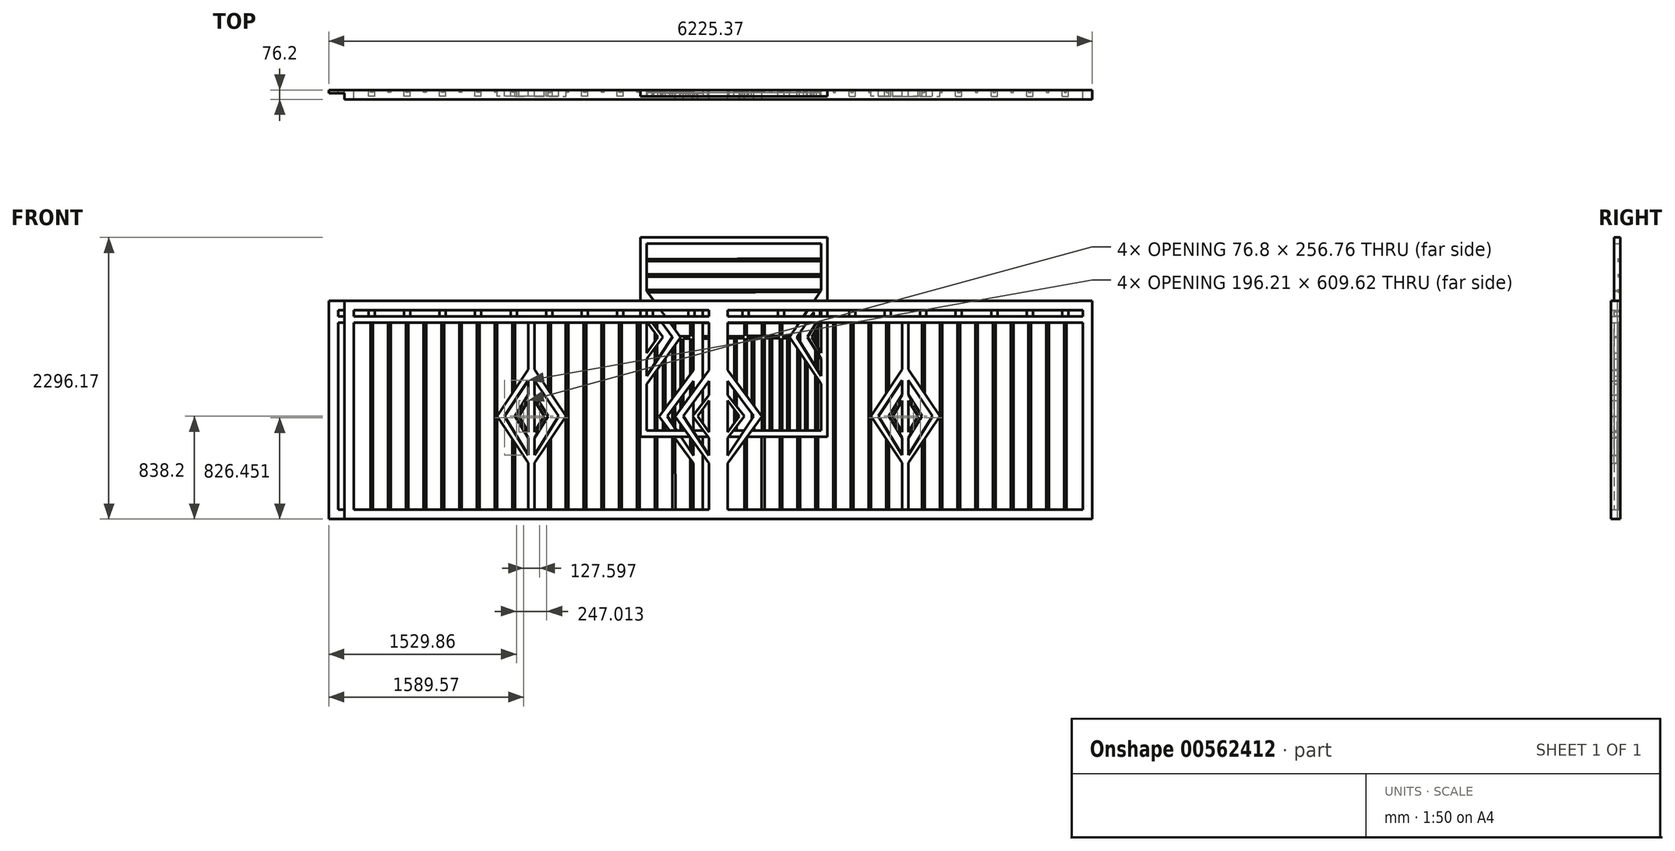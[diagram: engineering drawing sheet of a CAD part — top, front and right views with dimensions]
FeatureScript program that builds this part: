
annotation { "Feature Type Name" : "Feature", "Feature Type Description" : "" }
export const myFeature = defineFeature(function(context is Context, id is Id, definition is map)
    precondition{}
    {
        {
            var Q0;
            Q0=qCreatedBy(makeId("Front.planeOp"),FACE);
            var sketch = newSketch(context, id + "F0", { "sketchPlane" : qUnion([Q0])});
            skLineSegment(sketch, "E0.bottom", {"start": v(0, 0) * mm, "end": v(3048, 0) * mm});
            skLineSegment(sketch, "E0.top", {"start": v(0, -1778) * mm, "end": v(3048, -1778) * mm});
            skLineSegment(sketch, "E0.left", {"start": v(0, 0) * mm, "end": v(0, -1778) * mm});
            skLineSegment(sketch, "E0.right", {"start": v(3048, 0) * mm, "end": v(3048, -1778) * mm});
            skLineSegment(sketch, "E1.0", {"start": v(76.2, -76.2) * mm, "end": v(2971.8, -76.2) * mm});
            skLineSegment(sketch, "E1.1", {"start": v(76.2, -76.2) * mm, "end": v(76.2, -127) * mm});
            skLineSegment(sketch, "E1.2", {"start": v(76.2, -1701.8) * mm, "end": v(2971.8, -1701.8) * mm});
            skLineSegment(sketch, "E1.3", {"start": v(2971.8, -76.2) * mm, "end": v(2971.8, -127) * mm});
            skLineSegment(sketch, "E2.0", {"start": v(76.2, -127) * mm, "end": v(2971.8, -127) * mm});
            skLineSegment(sketch, "E3.0", {"start": v(76.2, -177.8) * mm, "end": v(2971.8, -177.8) * mm});
            skLineSegment(sketch, "E4.trimOffspring", {"start": v(76.2, -177.8) * mm, "end": v(76.2, -563.9) * mm});
            skLineSegment(sketch, "E5.trimOffspring", {"start": v(2971.8, -177.8) * mm, "end": v(2971.8, -1701.8) * mm});
            skLineSegment(sketch, "E6.0", {"start": v(1549.4, -177.8) * mm, "end": v(1549.4, -558.8) * mm});
            skLineSegment(sketch, "E7.0", {"start": v(2238.83, -177.8) * mm, "end": v(2238.83, -1701.8) * mm});
            skLineSegment(sketch, "E8.0", {"start": v(2257.88, -177.8) * mm, "end": v(2257.88, -1701.8) * mm});
            skLineSegment(sketch, "E9.1.0.0", {"start": v(2402.66, -177.8) * mm, "end": v(2402.66, -1701.8) * mm});
            skLineSegment(sketch, "E9.1.0.1", {"start": v(2383.61, -177.8) * mm, "end": v(2383.61, -1701.8) * mm});
            skLineSegment(sketch, "E9.2.0.0", {"start": v(2547.44, -177.8) * mm, "end": v(2547.44, -1701.8) * mm});
            skLineSegment(sketch, "E9.2.0.1", {"start": v(2528.4, -177.8) * mm, "end": v(2528.4, -1701.8) * mm});
            skLineSegment(sketch, "E9.3.0.0", {"start": v(2692.22, -177.8) * mm, "end": v(2692.22, -1701.8) * mm});
            skLineSegment(sketch, "E9.3.0.1", {"start": v(2673.17, -177.8) * mm, "end": v(2673.17, -1701.8) * mm});
            skLineSegment(sketch, "E9.4.0.0", {"start": v(2837, -177.8) * mm, "end": v(2837, -1701.8) * mm});
            skLineSegment(sketch, "E9.4.0.1", {"start": v(2817.95, -177.8) * mm, "end": v(2817.95, -1701.8) * mm});
            skLineSegment(sketch, "E9.direction1", {"start": v(2257.88, -1701.8) * mm, "end": v(2402.66, -1701.8) * mm, "construction": true});
            skLineSegment(sketch, "E10.MirrorCS", {"start": v(1949.27, -177.8) * mm, "end": v(1949.27, -1701.8) * mm});
            skLineSegment(sketch, "E11.MirrorCS", {"start": v(1659.71, -177.8) * mm, "end": v(1659.71, -723.56) * mm});
            skLineSegment(sketch, "E12.MirrorCS", {"start": v(2094.05, -177.8) * mm, "end": v(2094.05, -1701.8) * mm});
            skLineSegment(sketch, "E13.MirrorCS", {"start": v(2113.1, -177.8) * mm, "end": v(2113.1, -1701.8) * mm});
            skLineSegment(sketch, "E14.MirrorCS", {"start": v(1804.5, -177.8) * mm, "end": v(1804.5, -1701.8) * mm});
            skLineSegment(sketch, "E15.MirrorCS", {"start": v(1678.76, -177.8) * mm, "end": v(1678.76, -752.01) * mm});
            skLineSegment(sketch, "E16.MirrorCS", {"start": v(1968.32, -177.8) * mm, "end": v(1968.32, -1701.8) * mm});
            skLineSegment(sketch, "E17.MirrorCS", {"start": v(1823.54, -177.8) * mm, "end": v(1823.54, -1701.8) * mm});
            skLineSegment(sketch, "E18", {"start": v(1549.4, -558.8) * mm, "end": v(1804.5, -939.8) * mm});
            skLineSegment(sketch, "E19.MirrorCS", {"start": v(1549.4, -1320.8) * mm, "end": v(1804.5, -939.8) * mm});
            skLineSegment(sketch, "E20.MirrorCS", {"start": v(809.17, -177.8) * mm, "end": v(809.17, -1701.8) * mm});
            skLineSegment(sketch, "E21.MirrorCS", {"start": v(519.6, -177.8) * mm, "end": v(519.6, -1701.8) * mm});
            skLineSegment(sketch, "E22.MirrorCS", {"start": v(934.9, -177.8) * mm, "end": v(934.9, -1701.8) * mm});
            skLineSegment(sketch, "E23.MirrorCS", {"start": v(1243.5, -177.8) * mm, "end": v(1243.5, -1701.8) * mm});
            skLineSegment(sketch, "E24.MirrorCS", {"start": v(211, -177.8) * mm, "end": v(211, -746.81) * mm});
            skLineSegment(sketch, "E25.MirrorCS", {"start": v(953.95, -177.8) * mm, "end": v(953.95, -1701.8) * mm});
            skLineSegment(sketch, "E26.MirrorCS", {"start": v(374.83, -177.8) * mm, "end": v(374.83, -1701.8) * mm});
            skLineSegment(sketch, "E27.MirrorCS", {"start": v(1369.24, -177.8) * mm, "end": v(1369.24, -752.01) * mm});
            skLineSegment(sketch, "E28.MirrorCS", {"start": v(1498.6, -177.8) * mm, "end": v(1498.6, -558.8) * mm});
            skLineSegment(sketch, "E29.MirrorCS", {"start": v(645.34, -177.8) * mm, "end": v(645.34, -1701.8) * mm});
            skLineSegment(sketch, "E30.MirrorCS", {"start": v(500.56, -177.8) * mm, "end": v(500.56, -1701.8) * mm});
            skLineSegment(sketch, "E31.MirrorCS", {"start": v(1388.29, -177.8) * mm, "end": v(1388.29, -723.56) * mm});
            skLineSegment(sketch, "E32.MirrorCS", {"start": v(1079.68, -177.8) * mm, "end": v(1079.68, -1701.8) * mm});
            skLineSegment(sketch, "E33.MirrorCS", {"start": v(790.12, -177.8) * mm, "end": v(790.12, -1701.8) * mm});
            skLineSegment(sketch, "E34.MirrorCS", {"start": v(1224.46, -177.8) * mm, "end": v(1224.46, -1701.8) * mm});
            skLineSegment(sketch, "E35.MirrorCS", {"start": v(664.39, -177.8) * mm, "end": v(664.39, -1701.8) * mm});
            skLineSegment(sketch, "E36.MirrorCS", {"start": v(1098.73, -177.8) * mm, "end": v(1098.73, -1701.8) * mm});
            skLineSegment(sketch, "E37.MirrorCS", {"start": v(230.05, -177.8) * mm, "end": v(230.05, -772.66) * mm});
            skLineSegment(sketch, "E38.MirrorCS", {"start": v(355.78, -177.8) * mm, "end": v(352, -1703.62) * mm});
            skLineSegment(sketch, "E39", {"start": v(1549.4, -646.74) * mm, "end": v(1745.61, -939.8) * mm});
            skLineSegment(sketch, "E40", {"start": v(1745.61, -939.8) * mm, "end": v(1549.4, -1256.36) * mm});
            skLineSegment(sketch, "E41", {"start": v(1549.4, -811.42) * mm, "end": v(1626.2, -939.8) * mm});
            skLineSegment(sketch, "E42", {"start": v(1626.2, -939.8) * mm, "end": v(1549.4, -1068.18) * mm});
            skPoint(sketch, "E43.MirrorCS.end.orphan", {"position": v(1388.29, -939.8) * mm});
            skPoint(sketch, "E43.MirrorCS.start.orphan", {"position": v(1498.6, -1193.8) * mm});
            skPoint(sketch, "E44.MirrorCS.start.orphan", {"position": v(1498.6, -685.8) * mm});
            skPoint(sketch, "E45.orphan", {"position": v(1498.6, -558.8) * mm});
            skLineSegment(sketch, "E46", {"start": v(1549.4, -764.15) * mm, "end": v(1659.71, -939.8) * mm});
            skLineSegment(sketch, "E47", {"start": v(1659.71, -939.8) * mm, "end": v(1549.4, -1116.04) * mm});
            skLineSegment(sketch, "E48.MirrorCS", {"start": v(1421.8, -939.8) * mm, "end": v(1498.6, -1068.18) * mm});
            skLineSegment(sketch, "E49.MirrorCS", {"start": v(1388.29, -939.8) * mm, "end": v(1498.6, -1116.04) * mm});
            skLineSegment(sketch, "E50.MirrorCS", {"start": v(1498.6, -764.15) * mm, "end": v(1388.29, -939.8) * mm});
            skLineSegment(sketch, "E51.MirrorCS", {"start": v(1498.6, -811.42) * mm, "end": v(1421.8, -939.8) * mm});
            skLineSegment(sketch, "E52.MirrorCS", {"start": v(1498.6, -646.74) * mm, "end": v(1302.39, -939.8) * mm});
            skLineSegment(sketch, "E53.MirrorCS", {"start": v(1498.6, -558.8) * mm, "end": v(1243.5, -939.8) * mm});
            skLineSegment(sketch, "E54.MirrorCS", {"start": v(1498.6, -1320.8) * mm, "end": v(1243.5, -939.8) * mm});
            skLineSegment(sketch, "E55.MirrorCS", {"start": v(1302.39, -939.8) * mm, "end": v(1498.6, -1256.36) * mm});
            skLineSegment(sketch, "E56", {"start": v(76.2, -563.9) * mm, "end": v(353.89, -940.71) * mm});
            skLineSegment(sketch, "E57.MirrorCS", {"start": v(76.2, -1322.42) * mm, "end": v(353.89, -940.71) * mm});
            skLineSegment(sketch, "E58", {"start": v(74.38, -649.7) * mm, "end": v(288.17, -939.8) * mm});
            skLineSegment(sketch, "E59", {"start": v(288.17, -939.8) * mm, "end": v(76.2, -1257.98) * mm});
            skLineSegment(sketch, "E60", {"start": v(76.2, -813.05) * mm, "end": v(170.03, -939.8) * mm});
            skLineSegment(sketch, "E61", {"start": v(170.03, -939.8) * mm, "end": v(76.2, -1069.8) * mm});
            skLineSegment(sketch, "E62", {"start": v(76.2, -765.77) * mm, "end": v(211, -939.8) * mm});
            skLineSegment(sketch, "E63", {"start": v(211, -939.8) * mm, "end": v(76.2, -1117.66) * mm});
            skLineSegment(sketch, "E64.0", {"start": v(2852.88, -127) * mm, "end": v(2852.88, -76.2) * mm});
            skLineSegment(sketch, "E65.0", {"start": v(2802.08, -127) * mm, "end": v(2802.08, -76.2) * mm});
            skLineSegment(sketch, "E66.0", {"start": v(2563.32, -127) * mm, "end": v(2563.32, -76.2) * mm});
            skLineSegment(sketch, "E67.0", {"start": v(2512.52, -127) * mm, "end": v(2512.52, -76.2) * mm});
            skLineSegment(sketch, "E68.1.0.0", {"start": v(2222.96, -127) * mm, "end": v(2222.96, -76.2) * mm});
            skLineSegment(sketch, "E68.1.0.1", {"start": v(2273.76, -127) * mm, "end": v(2273.76, -76.2) * mm});
            skLineSegment(sketch, "E68.2.0.0", {"start": v(1933.4, -127) * mm, "end": v(1933.4, -76.2) * mm});
            skLineSegment(sketch, "E68.2.0.1", {"start": v(1984.2, -127) * mm, "end": v(1984.2, -76.2) * mm});
            skLineSegment(sketch, "E68.3.0.0", {"start": v(1643.84, -127) * mm, "end": v(1643.84, -76.2) * mm});
            skLineSegment(sketch, "E68.3.0.1", {"start": v(1694.64, -127) * mm, "end": v(1694.64, -76.2) * mm});
            skLineSegment(sketch, "E68.4.0.0", {"start": v(1354.28, -127) * mm, "end": v(1354.28, -76.2) * mm});
            skLineSegment(sketch, "E68.4.0.1", {"start": v(1405.08, -127) * mm, "end": v(1405.08, -76.2) * mm});
            skLineSegment(sketch, "E68.5.0.0", {"start": v(1064.72, -127) * mm, "end": v(1064.72, -76.2) * mm});
            skLineSegment(sketch, "E68.5.0.1", {"start": v(1115.52, -127) * mm, "end": v(1115.52, -76.2) * mm});
            skLineSegment(sketch, "E68.6.0.0", {"start": v(775.16, -127) * mm, "end": v(775.16, -76.2) * mm});
            skLineSegment(sketch, "E68.6.0.1", {"start": v(825.96, -127) * mm, "end": v(825.96, -76.2) * mm});
            skLineSegment(sketch, "E68.7.0.0", {"start": v(485.6, -127) * mm, "end": v(485.6, -76.2) * mm});
            skLineSegment(sketch, "E68.7.0.1", {"start": v(536.4, -127) * mm, "end": v(536.4, -76.2) * mm});
            skLineSegment(sketch, "E68.8.0.0", {"start": v(196.04, -127) * mm, "end": v(196.04, -76.2) * mm});
            skLineSegment(sketch, "E68.8.0.1", {"start": v(246.84, -127) * mm, "end": v(246.84, -76.2) * mm});
            skLineSegment(sketch, "E68.direction1", {"start": v(2512.52, -127) * mm, "end": v(2222.96, -127) * mm, "construction": true});
            skLineSegment(sketch, "E69", {"start": v(-64.68, 459.45) * mm, "end": v(-64.68, -2374.18) * mm});
            skLineSegment(sketch, "E70.trimOffspring", {"start": v(1388.29, -1156.04) * mm, "end": v(1388.29, -1701.8) * mm});
            skLineSegment(sketch, "E71.trimOffspring", {"start": v(1369.24, -1127.59) * mm, "end": v(1369.24, -1701.8) * mm});
            skLineSegment(sketch, "E72.trimOffspring", {"start": v(1659.71, -1156.04) * mm, "end": v(1659.71, -1701.8) * mm});
            skLineSegment(sketch, "E73.trimOffspring", {"start": v(1678.76, -1127.59) * mm, "end": v(1678.76, -1701.8) * mm});
            skLineSegment(sketch, "E74.trimOffspring", {"start": v(1498.6, -646.74) * mm, "end": v(1498.6, -764.15) * mm});
            skLineSegment(sketch, "E75.trimOffspring", {"start": v(1549.4, -646.74) * mm, "end": v(1549.4, -764.15) * mm});
            skLineSegment(sketch, "E76.trimOffspring", {"start": v(1498.6, -811.42) * mm, "end": v(1498.6, -1068.18) * mm});
            skLineSegment(sketch, "E77.trimOffspring", {"start": v(1549.4, -811.42) * mm, "end": v(1549.4, -1068.18) * mm});
            skLineSegment(sketch, "E78.trimOffspring", {"start": v(1498.6, -1116.04) * mm, "end": v(1498.6, -1256.36) * mm});
            skLineSegment(sketch, "E79.trimOffspring", {"start": v(1549.4, -1116.04) * mm, "end": v(1549.4, -1256.36) * mm});
            skLineSegment(sketch, "E80.trimOffspring", {"start": v(1498.6, -1320.8) * mm, "end": v(1498.6, -1701.8) * mm});
            skLineSegment(sketch, "E81.trimOffspring", {"start": v(1549.4, -1320.8) * mm, "end": v(1549.4, -1701.8) * mm});
            skLineSegment(sketch, "E82.trimOffspring", {"start": v(230.05, -1110.94) * mm, "end": v(230.05, -1701.8) * mm});
            skLineSegment(sketch, "E83.trimOffspring", {"start": v(211, -1137.13) * mm, "end": v(211, -1701.8) * mm});
            skLineSegment(sketch, "E84.trimOffspring", {"start": v(76.2, -652.17) * mm, "end": v(76.2, -765.77) * mm});
            skLineSegment(sketch, "E85.trimOffspring", {"start": v(76.2, -813.05) * mm, "end": v(76.2, -1069.8) * mm});
            skLineSegment(sketch, "E86.trimOffspring", {"start": v(76.2, -1117.66) * mm, "end": v(76.2, -1701.8) * mm});
            skLineSegment(sketch, "E87.MirrorCS", {"start": v(-3101.17, -76.2) * mm, "end": v(-3101.17, -127) * mm});
            skLineSegment(sketch, "E88.MirrorCS", {"start": v(-1627.97, -646.74) * mm, "end": v(-1627.97, -764.15) * mm});
            skLineSegment(sketch, "E89.MirrorCS", {"start": v(-1678.77, -646.74) * mm, "end": v(-1678.77, -764.15) * mm});
            skLineSegment(sketch, "E90.MirrorCS", {"start": v(-1627.97, -1116.04) * mm, "end": v(-1627.97, -1256.36) * mm});
            skLineSegment(sketch, "E91.MirrorCS", {"start": v(-1678.77, -1116.04) * mm, "end": v(-1678.77, -1256.36) * mm});
            skLineSegment(sketch, "E92.MirrorCS", {"start": v(-2692.69, -127) * mm, "end": v(-2692.69, -76.2) * mm});
            skLineSegment(sketch, "E93.MirrorCS", {"start": v(-1627.97, -764.15) * mm, "end": v(-1517.66, -939.8) * mm});
            skLineSegment(sketch, "E94.MirrorCS", {"start": v(-2641.89, -127) * mm, "end": v(-2641.89, -76.2) * mm});
            skLineSegment(sketch, "E95.MirrorCS", {"start": v(-1627.97, -811.42) * mm, "end": v(-1551.17, -939.8) * mm});
            skLineSegment(sketch, "E96.MirrorCS", {"start": v(-2062.77, -127) * mm, "end": v(-2062.77, -76.2) * mm});
            skLineSegment(sketch, "E97.MirrorCS", {"start": v(-205.57, -76.2) * mm, "end": v(-205.57, -127) * mm});
            skLineSegment(sketch, "E98.MirrorCS", {"start": v(-205.57, -652.17) * mm, "end": v(-205.57, -765.77) * mm});
            skLineSegment(sketch, "E99.MirrorCS", {"start": v(-2352.33, -127) * mm, "end": v(-2352.33, -76.2) * mm});
            skLineSegment(sketch, "E100.MirrorCS", {"start": v(-1773.2, -127) * mm, "end": v(-1773.2, -76.2) * mm});
            skLineSegment(sketch, "E101.MirrorCS", {"start": v(-2403.13, -127) * mm, "end": v(-2403.13, -76.2) * mm});
            skLineSegment(sketch, "E102.MirrorCS", {"start": v(-2113.57, -127) * mm, "end": v(-2113.57, -76.2) * mm});
            skLineSegment(sketch, "E103.MirrorCS", {"start": v(-205.57, -813.05) * mm, "end": v(-299.4, -939.8) * mm});
            skLineSegment(sketch, "E104.MirrorCS", {"start": v(-1678.77, -811.42) * mm, "end": v(-1755.57, -939.8) * mm});
            skLineSegment(sketch, "E105.MirrorCS", {"start": v(-2368.2, -177.8) * mm, "end": v(-2368.2, -1701.8) * mm});
            skLineSegment(sketch, "E106.MirrorCS", {"start": v(-299.4, -939.8) * mm, "end": v(-205.57, -1069.8) * mm});
            skLineSegment(sketch, "E107.MirrorCS", {"start": v(-1755.57, -939.8) * mm, "end": v(-1678.77, -1068.18) * mm});
            skLineSegment(sketch, "E108.MirrorCS", {"start": v(-904.53, -127) * mm, "end": v(-904.53, -76.2) * mm});
            skLineSegment(sketch, "E109.MirrorCS", {"start": v(-955.33, -127) * mm, "end": v(-955.33, -76.2) * mm});
            skLineSegment(sketch, "E110.MirrorCS", {"start": v(-614.97, -127) * mm, "end": v(-614.97, -76.2) * mm});
            skLineSegment(sketch, "E111.MirrorCS", {"start": v(-1551.17, -939.8) * mm, "end": v(-1627.97, -1068.18) * mm});
            skLineSegment(sketch, "E112.MirrorCS", {"start": v(-665.77, -127) * mm, "end": v(-665.77, -76.2) * mm});
            skLineSegment(sketch, "E113.MirrorCS", {"start": v(-1517.66, -939.8) * mm, "end": v(-1627.97, -1116.04) * mm});
            skLineSegment(sketch, "E114.MirrorCS", {"start": v(-359.42, -1110.94) * mm, "end": v(-359.42, -1701.8) * mm});
            skLineSegment(sketch, "E115.MirrorCS", {"start": v(-325.4, -127) * mm, "end": v(-325.4, -76.2) * mm});
            skLineSegment(sketch, "E116.MirrorCS", {"start": v(-376.2, -127) * mm, "end": v(-376.2, -76.2) * mm});
            skLineSegment(sketch, "E117.MirrorCS", {"start": v(-205.57, -1701.8) * mm, "end": v(-3101.17, -1701.8) * mm});
            skLineSegment(sketch, "E118.MirrorCS", {"start": v(-205.57, -127) * mm, "end": v(-3101.17, -127) * mm});
            skLineSegment(sketch, "E119.MirrorCS", {"start": v(-205.57, -177.8) * mm, "end": v(-3101.17, -177.8) * mm});
            skLineSegment(sketch, "E120.MirrorCS", {"start": v(-2641.89, -127) * mm, "end": v(-2352.33, -127) * mm, "construction": true});
            skLineSegment(sketch, "E121.MirrorCS", {"start": v(-359.42, -177.8) * mm, "end": v(-359.42, -772.66) * mm});
            skLineSegment(sketch, "E122.MirrorCS", {"start": v(-1824, -127) * mm, "end": v(-1824, -76.2) * mm});
            skLineSegment(sketch, "E123.MirrorCS", {"start": v(-2387.25, -1701.8) * mm, "end": v(-2532.03, -1701.8) * mm, "construction": true});
            skLineSegment(sketch, "E124.MirrorCS", {"start": v(-1483.65, -127) * mm, "end": v(-1483.65, -76.2) * mm});
            skPoint(sketch, "E125.MirrorP", {"position": v(-1517.66, -939.8) * mm});
            skLineSegment(sketch, "E126.MirrorCS", {"start": v(-1534.45, -127) * mm, "end": v(-1534.45, -76.2) * mm});
            skLineSegment(sketch, "E127.MirrorCS", {"start": v(-1194.09, -127) * mm, "end": v(-1194.09, -76.2) * mm});
            skLineSegment(sketch, "E128.MirrorCS", {"start": v(-1228.1, -177.8) * mm, "end": v(-1228.1, -1701.8) * mm});
            skLineSegment(sketch, "E129.MirrorCS", {"start": v(-1244.89, -127) * mm, "end": v(-1244.89, -76.2) * mm});
            skLineSegment(sketch, "E130.MirrorCS", {"start": v(-2802.54, -177.8) * mm, "end": v(-2802.54, -1701.8) * mm});
            skLineSegment(sketch, "E131.MirrorCS", {"start": v(-938.54, -177.8) * mm, "end": v(-938.54, -1701.8) * mm});
            skLineSegment(sketch, "E132.MirrorCS", {"start": v(-774.7, -177.8) * mm, "end": v(-774.7, -1701.8) * mm});
            skLineSegment(sketch, "E133.MirrorCS", {"start": v(-2982.25, -127) * mm, "end": v(-2982.25, -76.2) * mm});
            skLineSegment(sketch, "E134.MirrorCS", {"start": v(-2931.45, -127) * mm, "end": v(-2931.45, -76.2) * mm});
            skLineSegment(sketch, "E135.MirrorCS", {"start": v(-1517.66, -177.8) * mm, "end": v(-1517.66, -723.56) * mm});
            skLineSegment(sketch, "E136.MirrorCS", {"start": v(-2097.7, -177.8) * mm, "end": v(-2097.7, -1701.8) * mm});
            skLineSegment(sketch, "E137.MirrorCS", {"start": v(-340.37, -1137.13) * mm, "end": v(-340.37, -1701.8) * mm});
            skLineSegment(sketch, "E138.MirrorCS", {"start": v(-1209.05, -177.8) * mm, "end": v(-1209.05, -1701.8) * mm});
            skLineSegment(sketch, "E139.MirrorCS", {"start": v(-1952.91, -177.8) * mm, "end": v(-1952.91, -1701.8) * mm});
            skLineSegment(sketch, "E140.MirrorCS", {"start": v(-2512.98, -177.8) * mm, "end": v(-2512.98, -1701.8) * mm});
            skLineSegment(sketch, "E141.MirrorCS", {"start": v(-1498.6, -1127.59) * mm, "end": v(-1498.6, -1701.8) * mm});
            skLineSegment(sketch, "E142.MirrorCS", {"start": v(-2387.25, -177.8) * mm, "end": v(-2387.25, -1701.8) * mm});
            skLineSegment(sketch, "E143.MirrorCS", {"start": v(-2532.03, -177.8) * mm, "end": v(-2532.03, -1701.8) * mm});
            skLineSegment(sketch, "E144.MirrorCS", {"start": v(-793.76, -177.8) * mm, "end": v(-793.76, -1701.8) * mm});
            skLineSegment(sketch, "E145.MirrorCS", {"start": v(-129.37, 0) * mm, "end": v(-3177.37, 0) * mm});
            skLineSegment(sketch, "E146.MirrorCS", {"start": v(-129.37, -1778) * mm, "end": v(-3177.37, -1778) * mm});
            skLineSegment(sketch, "E147.MirrorCS", {"start": v(-2821.6, -177.8) * mm, "end": v(-2821.6, -1701.8) * mm});
            skLineSegment(sketch, "E148.MirrorCS", {"start": v(-205.57, -1117.66) * mm, "end": v(-205.57, -1701.8) * mm});
            skLineSegment(sketch, "E149.MirrorCS", {"start": v(-1517.66, -1156.04) * mm, "end": v(-1517.66, -1701.8) * mm});
            skLineSegment(sketch, "E150.MirrorCS", {"start": v(-1627.97, -1320.8) * mm, "end": v(-1372.88, -939.8) * mm});
            skLineSegment(sketch, "E151.MirrorCS", {"start": v(-129.37, 0) * mm, "end": v(-129.37, -1778) * mm});
            skLineSegment(sketch, "E152.MirrorCS", {"start": v(-3177.37, 0) * mm, "end": v(-3177.37, -1778) * mm});
            skLineSegment(sketch, "E153.MirrorCS", {"start": v(-205.57, -76.2) * mm, "end": v(-3101.17, -76.2) * mm});
            skLineSegment(sketch, "E154.MirrorCS", {"start": v(-205.57, -177.8) * mm, "end": v(-205.57, -563.9) * mm});
            skLineSegment(sketch, "E155.MirrorCS", {"start": v(-3101.17, -177.8) * mm, "end": v(-3101.17, -1701.8) * mm});
            skLineSegment(sketch, "E156.MirrorCS", {"start": v(-919.49, -177.8) * mm, "end": v(-919.49, -1701.8) * mm});
            skLineSegment(sketch, "E157.MirrorCS", {"start": v(-1678.77, -558.8) * mm, "end": v(-1933.86, -939.8) * mm});
            skLineSegment(sketch, "E158.MirrorCS", {"start": v(-2676.81, -177.8) * mm, "end": v(-2676.81, -1701.8) * mm});
            skLineSegment(sketch, "E159.MirrorCS", {"start": v(-1678.77, -177.8) * mm, "end": v(-1678.77, -558.8) * mm});
            skLineSegment(sketch, "E160.MirrorCS", {"start": v(-1431.76, -939.8) * mm, "end": v(-1627.97, -1256.36) * mm});
            skLineSegment(sketch, "E161.MirrorCS", {"start": v(-1627.97, -646.74) * mm, "end": v(-1431.76, -939.8) * mm});
            skLineSegment(sketch, "E162.MirrorCS", {"start": v(-1064.27, -177.8) * mm, "end": v(-1064.27, -1701.8) * mm});
            skLineSegment(sketch, "E163.MirrorCS", {"start": v(-2966.37, -177.8) * mm, "end": v(-2966.37, -1701.8) * mm});
            skLineSegment(sketch, "E164.MirrorCS", {"start": v(-1789.08, -1156.04) * mm, "end": v(-1789.08, -1701.8) * mm});
            skLineSegment(sketch, "E165.MirrorCS", {"start": v(-205.57, -563.9) * mm, "end": v(-483.26, -940.71) * mm});
            skLineSegment(sketch, "E166.MirrorCS", {"start": v(-485.15, -177.8) * mm, "end": v(-481.37, -1703.62) * mm});
            skLineSegment(sketch, "E167.MirrorCS", {"start": v(-1372.88, -177.8) * mm, "end": v(-1372.88, -1701.8) * mm});
            skLineSegment(sketch, "E168.MirrorCS", {"start": v(-2947.32, -177.8) * mm, "end": v(-2947.32, -1701.8) * mm});
            skLineSegment(sketch, "E169.MirrorCS", {"start": v(-1808.13, -1127.59) * mm, "end": v(-1808.13, -1701.8) * mm});
            skLineSegment(sketch, "E170.MirrorCS", {"start": v(-205.57, -1322.42) * mm, "end": v(-483.26, -940.71) * mm});
            skLineSegment(sketch, "E171.MirrorCS", {"start": v(-205.57, -813.05) * mm, "end": v(-205.57, -1069.8) * mm});
            skLineSegment(sketch, "E172.MirrorCS", {"start": v(-203.75, -649.7) * mm, "end": v(-417.54, -939.8) * mm});
            skLineSegment(sketch, "E173.MirrorCS", {"start": v(-1678.77, -646.74) * mm, "end": v(-1874.98, -939.8) * mm});
            skLineSegment(sketch, "E174.MirrorCS", {"start": v(-1627.97, -558.8) * mm, "end": v(-1372.88, -939.8) * mm});
            skLineSegment(sketch, "E175.MirrorCS", {"start": v(-340.37, -177.8) * mm, "end": v(-340.37, -746.81) * mm});
            skLineSegment(sketch, "E176.MirrorCS", {"start": v(-2078.64, -177.8) * mm, "end": v(-2078.64, -1701.8) * mm});
            skLineSegment(sketch, "E177.MirrorCS", {"start": v(-417.54, -939.8) * mm, "end": v(-205.57, -1257.98) * mm});
            skLineSegment(sketch, "E178.MirrorCS", {"start": v(-1874.98, -939.8) * mm, "end": v(-1678.77, -1256.36) * mm});
            skLineSegment(sketch, "E179.MirrorCS", {"start": v(-1083.32, -177.8) * mm, "end": v(-1083.32, -1701.8) * mm});
            skPoint(sketch, "E180.MirrorP", {"position": v(-1627.97, -1193.8) * mm});
            skLineSegment(sketch, "E181.MirrorCS", {"start": v(-1789.08, -177.8) * mm, "end": v(-1789.08, -723.56) * mm});
            skLineSegment(sketch, "E182.MirrorCS", {"start": v(-504.2, -177.8) * mm, "end": v(-504.2, -1701.8) * mm});
            skLineSegment(sketch, "E183.MirrorCS", {"start": v(-1627.97, -811.42) * mm, "end": v(-1627.97, -1068.18) * mm});
            skLineSegment(sketch, "E184.MirrorCS", {"start": v(-648.98, -177.8) * mm, "end": v(-648.98, -1701.8) * mm});
            skLineSegment(sketch, "E185.MirrorCS", {"start": v(-1498.6, -177.8) * mm, "end": v(-1498.6, -752.01) * mm});
            skLineSegment(sketch, "E186.MirrorCS", {"start": v(-1678.77, -811.42) * mm, "end": v(-1678.77, -1068.18) * mm});
            skLineSegment(sketch, "E187.MirrorCS", {"start": v(-2223.42, -177.8) * mm, "end": v(-2223.42, -1701.8) * mm});
            skLineSegment(sketch, "E188.MirrorCS", {"start": v(-1353.83, -177.8) * mm, "end": v(-1353.83, -1701.8) * mm});
            skLineSegment(sketch, "E189.MirrorCS", {"start": v(-205.57, -765.77) * mm, "end": v(-340.37, -939.8) * mm});
            skLineSegment(sketch, "E190.MirrorCS", {"start": v(-1678.77, -764.15) * mm, "end": v(-1789.08, -939.8) * mm});
            skLineSegment(sketch, "E191.MirrorCS", {"start": v(-1627.97, -177.8) * mm, "end": v(-1627.97, -558.8) * mm});
            skPoint(sketch, "E192.MirrorP", {"position": v(-1627.97, -685.8) * mm});
            skLineSegment(sketch, "E193.MirrorCS", {"start": v(-2242.47, -177.8) * mm, "end": v(-2242.47, -1701.8) * mm});
            skLineSegment(sketch, "E194.MirrorCS", {"start": v(-340.37, -939.8) * mm, "end": v(-205.57, -1117.66) * mm});
            skLineSegment(sketch, "E195.MirrorCS", {"start": v(-1789.08, -939.8) * mm, "end": v(-1678.77, -1116.04) * mm});
            skLineSegment(sketch, "E196.MirrorCS", {"start": v(-1678.77, -1320.8) * mm, "end": v(-1933.86, -939.8) * mm});
            skPoint(sketch, "E197.MirrorP", {"position": v(-1627.97, -558.8) * mm});
            skLineSegment(sketch, "E198.MirrorCS", {"start": v(-2657.76, -177.8) * mm, "end": v(-2657.76, -1701.8) * mm});
            skLineSegment(sketch, "E199.MirrorCS", {"start": v(-1933.86, -177.8) * mm, "end": v(-1933.86, -1701.8) * mm});
            skLineSegment(sketch, "E200.MirrorCS", {"start": v(-1627.97, -1320.8) * mm, "end": v(-1627.97, -1701.8) * mm});
            skLineSegment(sketch, "E201.MirrorCS", {"start": v(-629.93, -177.8) * mm, "end": v(-629.93, -1701.8) * mm});
            skLineSegment(sketch, "E202.MirrorCS", {"start": v(-1808.13, -177.8) * mm, "end": v(-1808.13, -752.01) * mm});
            skLineSegment(sketch, "E203.MirrorCS", {"start": v(-1678.77, -1320.8) * mm, "end": v(-1678.77, -1701.8) * mm});
            skLineSegment(sketch, "E204", {"start": v(76.2, -127) * mm, "end": v(0, -127) * mm});
            skSolve(sketch);
        }
        {
            var Q0;
            Q0=makeQuery(id+"F0.imprint","IMPRINT",FACE,{"disambiguationData":[TD([[makeQuery(id+"F0.imprint","IMPRINT",EDGE,{"derivedFrom":sQuery(id+"F0.wireOp",EDGE,"E0.bottom")}),-1.0]])]});
            extrude(context, id + "F1", {"entities" : qUnion([Q0]), "depth" : 76.2 * mm, "offsetDistance" : 25.4 * mm});
        }
        {
            var Q0;
            Q0 = qSketchRegion(id + "F0", true);
            extrude(context, id + "F2", {"entities" : qUnion([Q0]), "operationType" : NewBodyOperationType.ADD, "depth" : 25.4 * mm, "offsetDistance" : 25.4 * mm});
        }
        {
            var Q0;
            {var subQ0=sQuery(id+"F0.wireOp",EDGE,"E68.8.0.0");Q0=makeQuery(id+"F0.imprint","IMPRINT",FACE,{"disambiguationData":[TD([[makeQuery(id+"F0.imprint","IMPRINT",EDGE,{"derivedFrom":subQ0}),-1.0]])]});}
            var Q1;
            {var subQ0=sQuery(id+"F0.wireOp",EDGE,"E68.7.0.0");Q1=makeQuery(id+"F0.imprint","IMPRINT",FACE,{"disambiguationData":[TD([[makeQuery(id+"F0.imprint","IMPRINT",EDGE,{"derivedFrom":subQ0}),-1.0]])]});}
            var Q2;
            {var subQ0=sQuery(id+"F0.wireOp",EDGE,"E68.6.0.0");Q2=makeQuery(id+"F0.imprint","IMPRINT",FACE,{"disambiguationData":[TD([[makeQuery(id+"F0.imprint","IMPRINT",EDGE,{"derivedFrom":subQ0}),-1.0]])]});}
            var Q3;
            {var subQ0=sQuery(id+"F0.wireOp",EDGE,"E68.5.0.0");Q3=makeQuery(id+"F0.imprint","IMPRINT",FACE,{"disambiguationData":[TD([[makeQuery(id+"F0.imprint","IMPRINT",EDGE,{"derivedFrom":subQ0}),-1.0]])]});}
            var Q4;
            {var subQ0=sQuery(id+"F0.wireOp",EDGE,"E68.4.0.0");Q4=makeQuery(id+"F0.imprint","IMPRINT",FACE,{"disambiguationData":[TD([[makeQuery(id+"F0.imprint","IMPRINT",EDGE,{"derivedFrom":subQ0}),-1.0]])]});}
            var Q5;
            {var subQ0=sQuery(id+"F0.wireOp",EDGE,"E68.3.0.0");Q5=makeQuery(id+"F0.imprint","IMPRINT",FACE,{"disambiguationData":[TD([[makeQuery(id+"F0.imprint","IMPRINT",EDGE,{"derivedFrom":subQ0}),-1.0]])]});}
            var Q6;
            {var subQ0=sQuery(id+"F0.wireOp",EDGE,"E68.2.0.0");Q6=makeQuery(id+"F0.imprint","IMPRINT",FACE,{"disambiguationData":[TD([[makeQuery(id+"F0.imprint","IMPRINT",EDGE,{"derivedFrom":subQ0}),-1.0]])]});}
            var Q7;
            {var subQ0=sQuery(id+"F0.wireOp",EDGE,"E68.1.0.0");Q7=makeQuery(id+"F0.imprint","IMPRINT",FACE,{"disambiguationData":[TD([[makeQuery(id+"F0.imprint","IMPRINT",EDGE,{"derivedFrom":subQ0}),-1.0]])]});}
            var Q8;
            {var subQ0=sQuery(id+"F0.wireOp",EDGE,"E66.0");Q8=makeQuery(id+"F0.imprint","IMPRINT",FACE,{"disambiguationData":[TD([[makeQuery(id+"F0.imprint","IMPRINT",EDGE,{"derivedFrom":subQ0}),1.0]])]});}
            var Q9;
            {var subQ0=sQuery(id+"F0.wireOp",EDGE,"E64.0");Q9=makeQuery(id+"F0.imprint","IMPRINT",FACE,{"disambiguationData":[TD([[makeQuery(id+"F0.imprint","IMPRINT",EDGE,{"derivedFrom":subQ0}),1.0]])]});}
            extrude(context, id + "F3", {"entities" : qUnion([Q0, Q1, Q2, Q3, Q4, Q5, Q6, Q7, Q8, Q9]), "operationType" : NewBodyOperationType.ADD, "depth" : 50.8 * mm, "offsetDistance" : 25.4 * mm});
        }
        {
            var Q0;
            {var subQ7=sQuery(id+"F0.wireOp",EDGE,"E6.0");Q0=makeQuery(id+"F0.imprint","IMPRINT",FACE,{"disambiguationData":[TD([[makeQuery(id+"F0.imprint","IMPRINT",EDGE,{"derivedFrom":subQ7}),-1.0]])]});}
            extrude(context, id + "F4", {"entities" : qUnion([Q0]), "operationType" : NewBodyOperationType.ADD, "depth" : 50.8 * mm, "offsetDistance" : 25.4 * mm});
        }
        {
            var Q0;
            {var subQ0=sQuery(id+"F0.wireOp",EDGE,"E24.MirrorCS");Q0=makeQuery(id+"F0.imprint","IMPRINT",FACE,{"disambiguationData":[TD([[makeQuery(id+"F0.imprint","IMPRINT",EDGE,{"derivedFrom":subQ0}),1.0]])]});}
            var Q1;
            {var subQ0=sQuery(id+"F0.wireOp",EDGE,"E82.trimOffspring");Q1=makeQuery(id+"F0.imprint","IMPRINT",FACE,{"disambiguationData":[TD([[makeQuery(id+"F0.imprint","IMPRINT",EDGE,{"derivedFrom":subQ0}),-1.0]])]});}
            var Q2;
            {var subQ4=sQuery(id+"F0.wireOp",EDGE,"E26.MirrorCS");Q2=makeQuery(id+"F0.imprint","IMPRINT",FACE,{"disambiguationData":[TD([[makeQuery(id+"F0.imprint","IMPRINT",EDGE,{"derivedFrom":subQ4}),-1.0]])]});}
            var Q3;
            {var subQ0=sQuery(id+"F0.wireOp",EDGE,"E21.MirrorCS");Q3=makeQuery(id+"F0.imprint","IMPRINT",FACE,{"disambiguationData":[TD([[makeQuery(id+"F0.imprint","IMPRINT",EDGE,{"derivedFrom":subQ0}),-1.0]])]});}
            var Q4;
            {var subQ0=sQuery(id+"F0.wireOp",EDGE,"E29.MirrorCS");Q4=makeQuery(id+"F0.imprint","IMPRINT",FACE,{"disambiguationData":[TD([[makeQuery(id+"F0.imprint","IMPRINT",EDGE,{"derivedFrom":subQ0}),1.0]])]});}
            var Q5;
            {var subQ0=sQuery(id+"F0.wireOp",EDGE,"E20.MirrorCS");Q5=makeQuery(id+"F0.imprint","IMPRINT",FACE,{"disambiguationData":[TD([[makeQuery(id+"F0.imprint","IMPRINT",EDGE,{"derivedFrom":subQ0}),-1.0]])]});}
            var Q6;
            {var subQ0=sQuery(id+"F0.wireOp",EDGE,"E22.MirrorCS");Q6=makeQuery(id+"F0.imprint","IMPRINT",FACE,{"disambiguationData":[TD([[makeQuery(id+"F0.imprint","IMPRINT",EDGE,{"derivedFrom":subQ0}),1.0]])]});}
            var Q7;
            {var subQ0=sQuery(id+"F0.wireOp",EDGE,"E32.MirrorCS");Q7=makeQuery(id+"F0.imprint","IMPRINT",FACE,{"disambiguationData":[TD([[makeQuery(id+"F0.imprint","IMPRINT",EDGE,{"derivedFrom":subQ0}),1.0]])]});}
            var Q8;
            {var subQ6=sQuery(id+"F0.wireOp",EDGE,"E34.MirrorCS");Q8=makeQuery(id+"F0.imprint","IMPRINT",FACE,{"disambiguationData":[TD([[makeQuery(id+"F0.imprint","IMPRINT",EDGE,{"derivedFrom":subQ6}),1.0]])]});}
            var Q9;
            {var subQ0=sQuery(id+"F0.wireOp",EDGE,"E70.trimOffspring");Q9=makeQuery(id+"F0.imprint","IMPRINT",FACE,{"disambiguationData":[TD([[makeQuery(id+"F0.imprint","IMPRINT",EDGE,{"derivedFrom":subQ0}),-1.0]])]});}
            var Q10;
            {var subQ0=sQuery(id+"F0.wireOp",EDGE,"E27.MirrorCS");Q10=makeQuery(id+"F0.imprint","IMPRINT",FACE,{"disambiguationData":[TD([[makeQuery(id+"F0.imprint","IMPRINT",EDGE,{"derivedFrom":subQ0}),1.0]])]});}
            var Q11;
            {var subQ0=sQuery(id+"F0.wireOp",EDGE,"E11.MirrorCS");Q11=makeQuery(id+"F0.imprint","IMPRINT",FACE,{"disambiguationData":[TD([[makeQuery(id+"F0.imprint","IMPRINT",EDGE,{"derivedFrom":subQ0}),1.0]])]});}
            var Q12;
            {var subQ0=sQuery(id+"F0.wireOp",EDGE,"E72.trimOffspring");Q12=makeQuery(id+"F0.imprint","IMPRINT",FACE,{"disambiguationData":[TD([[makeQuery(id+"F0.imprint","IMPRINT",EDGE,{"derivedFrom":subQ0}),1.0]])]});}
            var Q13;
            {var subQ4=sQuery(id+"F0.wireOp",EDGE,"E17.MirrorCS");Q13=makeQuery(id+"F0.imprint","IMPRINT",FACE,{"disambiguationData":[TD([[makeQuery(id+"F0.imprint","IMPRINT",EDGE,{"derivedFrom":subQ4}),-1.0]])]});}
            var Q14;
            {var subQ0=sQuery(id+"F0.wireOp",EDGE,"E10.MirrorCS");Q14=makeQuery(id+"F0.imprint","IMPRINT",FACE,{"disambiguationData":[TD([[makeQuery(id+"F0.imprint","IMPRINT",EDGE,{"derivedFrom":subQ0}),1.0]])]});}
            var Q15;
            {var subQ0=sQuery(id+"F0.wireOp",EDGE,"E8.0");Q15=makeQuery(id+"F0.imprint","IMPRINT",FACE,{"disambiguationData":[TD([[makeQuery(id+"F0.imprint","IMPRINT",EDGE,{"derivedFrom":subQ0}),-1.0]])]});}
            var Q16;
            {var subQ0=sQuery(id+"F0.wireOp",EDGE,"E9.1.0.0");Q16=makeQuery(id+"F0.imprint","IMPRINT",FACE,{"disambiguationData":[TD([[makeQuery(id+"F0.imprint","IMPRINT",EDGE,{"derivedFrom":subQ0}),-1.0]])]});}
            var Q17;
            {var subQ0=sQuery(id+"F0.wireOp",EDGE,"E9.2.0.0");Q17=makeQuery(id+"F0.imprint","IMPRINT",FACE,{"disambiguationData":[TD([[makeQuery(id+"F0.imprint","IMPRINT",EDGE,{"derivedFrom":subQ0}),-1.0]])]});}
            var Q18;
            {var subQ0=sQuery(id+"F0.wireOp",EDGE,"E9.3.0.0");Q18=makeQuery(id+"F0.imprint","IMPRINT",FACE,{"disambiguationData":[TD([[makeQuery(id+"F0.imprint","IMPRINT",EDGE,{"derivedFrom":subQ0}),-1.0]])]});}
            var Q19;
            {var subQ0=sQuery(id+"F0.wireOp",EDGE,"E9.4.0.0");Q19=makeQuery(id+"F0.imprint","IMPRINT",FACE,{"disambiguationData":[TD([[makeQuery(id+"F0.imprint","IMPRINT",EDGE,{"derivedFrom":subQ0}),-1.0]])]});}
            var Q20;
            {var subQ0=sQuery(id+"F0.wireOp",EDGE,"E12.MirrorCS");Q20=makeQuery(id+"F0.imprint","IMPRINT",FACE,{"disambiguationData":[TD([[makeQuery(id+"F0.imprint","IMPRINT",EDGE,{"derivedFrom":subQ0}),1.0]])]});}
            extrude(context, id + "F5", {"entities" : qUnion([Q0, Q1, Q2, Q3, Q4, Q5, Q6, Q7, Q8, Q9, Q10, Q11, Q12, Q13, Q14, Q15, Q16, Q17, Q18, Q19, Q20]), "operationType" : NewBodyOperationType.ADD, "depth" : 19.05 * mm, "offsetDistance" : 25.4 * mm, "hasDraft" : true, "draftAngle" : 3 * degree});
        }
        {
            var Q0;
            Q0=makeQuery(id+"F1.opExtrude","SWEPT_BODY",BODY,{"disambiguationData":[OSD([sQuery(id+"F0.wireOp",EDGE,"E0.bottom"),sQuery(id+"F0.wireOp",EDGE,"E0.top"),sQuery(id+"F0.wireOp",EDGE,"E0.left"),sQuery(id+"F0.wireOp",EDGE,"E0.right"),sQuery(id+"F0.wireOp",EDGE,"E1.0"),sQuery(id+"F0.wireOp",EDGE,"E1.1"),sQuery(id+"F0.wireOp",EDGE,"E1.2"),sQuery(id+"F0.wireOp",EDGE,"E1.3"),sQuery(id+"F0.wireOp",EDGE,"E2.0"),sQuery(id+"F0.wireOp",EDGE,"E3.0"),sQuery(id+"F0.wireOp",EDGE,"E4.trimOffspring"),sQuery(id+"F0.wireOp",EDGE,"E5.trimOffspring"),sQuery(id+"F0.wireOp",EDGE,"E56"),sQuery(id+"F0.wireOp",EDGE,"E57.MirrorCS"),sQuery(id+"F0.wireOp",EDGE,"E58"),sQuery(id+"F0.wireOp",EDGE,"E59"),sQuery(id+"F0.wireOp",EDGE,"E60"),sQuery(id+"F0.wireOp",EDGE,"E61"),sQuery(id+"F0.wireOp",EDGE,"E62"),sQuery(id+"F0.wireOp",EDGE,"E63"),sQuery(id+"F0.wireOp",EDGE,"E84.trimOffspring"),sQuery(id+"F0.wireOp",EDGE,"E85.trimOffspring"),sQuery(id+"F0.wireOp",EDGE,"E86.trimOffspring")])]});
            var Q1;
            Q1=qCreatedBy(makeId("Right.planeOp"),FACE);
            mirror(context, id + "F6", {"entities" : qUnion([Q0]), "mirrorPlane" : qUnion([Q1])});
        }
        {
            var Q0;
            Q0=qCreatedBy(makeId("Front.planeOp"),FACE);
            var sketch = newSketch(context, id + "F7", { "sketchPlane" : qUnion([Q0])});
            skLineSegment(sketch, "E205.2", {"start": v(-586.5, -1056.63) * mm, "end": v(835.9, -1056.63) * mm});
            skLineSegment(sketch, "E206.0", {"start": v(-586.5, 518.17) * mm, "end": v(886.7, 518.17) * mm});
            skLineSegment(sketch, "E207.0", {"start": v(-586.5, 467.37) * mm, "end": v(835.9, 467.37) * mm});
            skLineSegment(sketch, "E208.trimOffspring", {"start": v(-586.5, 467.37) * mm, "end": v(-586.5, 81.27) * mm});
            skLineSegment(sketch, "E209.0", {"start": v(886.7, 467.37) * mm, "end": v(886.7, 86.37) * mm});
            skLineSegment(sketch, "E210.MirrorCS", {"start": v(835.9, 467.37) * mm, "end": v(835.9, 86.37) * mm});
            skPoint(sketch, "E211.MirrorCS.end.orphan", {"position": v(725.58, -294.63) * mm});
            skPoint(sketch, "E211.MirrorCS.start.orphan", {"position": v(835.9, -548.63) * mm});
            skPoint(sketch, "E212.MirrorCS.start.orphan", {"position": v(835.9, -40.63) * mm});
            skPoint(sketch, "E213.orphan", {"position": v(835.9, 86.37) * mm});
            skLineSegment(sketch, "E214.MirrorCS", {"start": v(759.1, -294.63) * mm, "end": v(835.9, -423) * mm});
            skLineSegment(sketch, "E215.MirrorCS", {"start": v(725.58, -294.63) * mm, "end": v(835.9, -470.86) * mm});
            skLineSegment(sketch, "E216.MirrorCS", {"start": v(835.9, -118.98) * mm, "end": v(725.58, -294.63) * mm});
            skLineSegment(sketch, "E217.MirrorCS", {"start": v(835.9, -166.25) * mm, "end": v(759.1, -294.63) * mm});
            skLineSegment(sketch, "E218.MirrorCS", {"start": v(835.9, -1.57) * mm, "end": v(639.68, -294.63) * mm});
            skLineSegment(sketch, "E219.MirrorCS", {"start": v(835.9, 86.37) * mm, "end": v(580.72, -294.75) * mm});
            skLineSegment(sketch, "E220.MirrorCS", {"start": v(835.9, -675.63) * mm, "end": v(580.8, -294.63) * mm});
            skLineSegment(sketch, "E221.MirrorCS", {"start": v(639.68, -294.63) * mm, "end": v(835.9, -611.19) * mm});
            skLineSegment(sketch, "E222", {"start": v(-586.5, 81.27) * mm, "end": v(-307.96, -296.71) * mm});
            skLineSegment(sketch, "E223.MirrorCS", {"start": v(-586.5, -677.25) * mm, "end": v(-307.96, -296.71) * mm});
            skLineSegment(sketch, "E224", {"start": v(-588.32, -4.53) * mm, "end": v(-374.54, -294.63) * mm});
            skLineSegment(sketch, "E225", {"start": v(-374.54, -294.63) * mm, "end": v(-586.5, -612.81) * mm});
            skLineSegment(sketch, "E226", {"start": v(-586.5, -167.87) * mm, "end": v(-492.67, -294.63) * mm});
            skLineSegment(sketch, "E227", {"start": v(-492.67, -294.63) * mm, "end": v(-586.5, -424.63) * mm});
            skLineSegment(sketch, "E228", {"start": v(-586.5, -120.6) * mm, "end": v(-451.7, -294.63) * mm});
            skLineSegment(sketch, "E229", {"start": v(-451.7, -294.63) * mm, "end": v(-586.5, -472.49) * mm});
            skLineSegment(sketch, "E230.trimOffspring", {"start": v(725.58, -510.87) * mm, "end": v(725.58, -1056.63) * mm});
            skLineSegment(sketch, "E231.trimOffspring", {"start": v(706.53, -482.42) * mm, "end": v(706.53, -1056.63) * mm});
            skLineSegment(sketch, "E232.trimOffspring", {"start": v(835.9, -1.57) * mm, "end": v(835.9, -118.98) * mm});
            skLineSegment(sketch, "E233.trimOffspring", {"start": v(886.7, -1.57) * mm, "end": v(886.7, -118.98) * mm});
            skLineSegment(sketch, "E234.trimOffspring", {"start": v(835.9, -166.25) * mm, "end": v(835.9, -423) * mm});
            skLineSegment(sketch, "E235.trimOffspring", {"start": v(886.7, -166.25) * mm, "end": v(886.7, -423) * mm});
            skLineSegment(sketch, "E236.trimOffspring", {"start": v(835.9, -470.86) * mm, "end": v(835.9, -611.19) * mm});
            skLineSegment(sketch, "E237.trimOffspring", {"start": v(886.7, -470.86) * mm, "end": v(886.7, -611.19) * mm});
            skLineSegment(sketch, "E238.trimOffspring", {"start": v(835.9, -675.63) * mm, "end": v(835.9, -1056.63) * mm});
            skLineSegment(sketch, "E239.trimOffspring", {"start": v(886.7, -675.63) * mm, "end": v(886.7, -1056.63) * mm});
            skLineSegment(sketch, "E240.trimOffspring", {"start": v(-432.66, -467.08) * mm, "end": v(-432.66, -1056.63) * mm});
            skLineSegment(sketch, "E241.trimOffspring", {"start": v(-451.7, -493.1) * mm, "end": v(-451.7, -1056.63) * mm});
            skLineSegment(sketch, "E242.trimOffspring", {"start": v(-586.5, -7) * mm, "end": v(-586.5, -120.6) * mm});
            skLineSegment(sketch, "E243.trimOffspring", {"start": v(-586.5, -167.87) * mm, "end": v(-586.5, -424.63) * mm});
            skLineSegment(sketch, "E244.trimOffspring", {"start": v(-586.5, -472.49) * mm, "end": v(-586.5, -1056.63) * mm});
            skLineSegment(sketch, "E245", {"start": v(886.7, -1132.83) * mm, "end": v(886.7, 518.17) * mm});
            skLineSegment(sketch, "E246", {"start": v(-586.5, 518.17) * mm, "end": v(-637.3, 518.17) * mm});
            skLineSegment(sketch, "E247.0", {"start": v(-637.3, 518.17) * mm, "end": v(-637.3, -1107.43) * mm});
            skLineSegment(sketch, "E248.0", {"start": v(-637.3, -1107.43) * mm, "end": v(886.7, -1107.43) * mm});
            skLineSegment(sketch, "E249.0", {"start": v(-315.15, -287.2) * mm, "end": v(586.85, -285.21) * mm});
            skLineSegment(sketch, "E250.0", {"start": v(-314.94, -306.25) * mm, "end": v(587.25, -304.26) * mm});
            skLineSegment(sketch, "E251.0.1.0", {"start": v(-315.15, -161.47) * mm, "end": v(586.85, -159.48) * mm});
            skLineSegment(sketch, "E251.0.1.1", {"start": v(-314.94, -180.52) * mm, "end": v(587.25, -178.53) * mm});
            skLineSegment(sketch, "E251.0.2.0", {"start": v(-315.15, -35.74) * mm, "end": v(586.85, -33.75) * mm});
            skLineSegment(sketch, "E251.0.2.1", {"start": v(-314.94, -54.8) * mm, "end": v(587.25, -52.8) * mm});
            skLineSegment(sketch, "E251.0.3.0", {"start": v(-315.15, 89.99) * mm, "end": v(586.85, 91.98) * mm});
            skLineSegment(sketch, "E251.0.3.1", {"start": v(-314.94, 70.94) * mm, "end": v(587.25, 72.93) * mm});
            skLineSegment(sketch, "E251.0.4.0", {"start": v(-315.15, 215.72) * mm, "end": v(586.85, 217.7) * mm});
            skLineSegment(sketch, "E251.0.4.1", {"start": v(-314.94, 196.67) * mm, "end": v(587.25, 198.66) * mm});
            skLineSegment(sketch, "E251.0.5.0", {"start": v(-315.15, 341.45) * mm, "end": v(586.85, 343.44) * mm});
            skLineSegment(sketch, "E251.0.5.1", {"start": v(-314.94, 322.4) * mm, "end": v(587.25, 324.39) * mm});
            skLineSegment(sketch, "E251.1.0.0", {"start": v(-289.75, -287.2) * mm, "end": v(587.07, -285.27) * mm});
            skLineSegment(sketch, "E251.1.0.1", {"start": v(-289.54, -306.25) * mm, "end": v(587.29, -304.32) * mm});
            skLineSegment(sketch, "E251.1.1.0", {"start": v(-289.75, -161.47) * mm, "end": v(612.25, -159.48) * mm});
            skLineSegment(sketch, "E251.1.1.1", {"start": v(-289.54, -180.52) * mm, "end": v(612.65, -178.53) * mm});
            skLineSegment(sketch, "E251.1.2.0", {"start": v(-289.75, -35.74) * mm, "end": v(612.25, -33.75) * mm});
            skLineSegment(sketch, "E251.1.2.1", {"start": v(-289.54, -54.8) * mm, "end": v(612.65, -52.8) * mm});
            skLineSegment(sketch, "E251.1.3.0", {"start": v(-289.75, 89.99) * mm, "end": v(612.25, 91.98) * mm});
            skLineSegment(sketch, "E251.1.3.1", {"start": v(-289.54, 70.94) * mm, "end": v(612.65, 72.93) * mm});
            skLineSegment(sketch, "E251.1.4.0", {"start": v(-289.75, 215.72) * mm, "end": v(612.25, 217.7) * mm});
            skLineSegment(sketch, "E251.1.4.1", {"start": v(-289.54, 196.67) * mm, "end": v(612.65, 198.66) * mm});
            skLineSegment(sketch, "E251.1.5.0", {"start": v(-289.75, 341.45) * mm, "end": v(612.25, 343.44) * mm});
            skLineSegment(sketch, "E251.1.5.1", {"start": v(-289.54, 322.4) * mm, "end": v(612.65, 324.39) * mm});
            skLineSegment(sketch, "E251.2.0.0", {"start": v(-264.35, -287.2) * mm, "end": v(587.03, -285.32) * mm});
            skLineSegment(sketch, "E251.2.0.1", {"start": v(-264.14, -306.25) * mm, "end": v(587.33, -304.37) * mm});
            skLineSegment(sketch, "E251.2.1.0", {"start": v(-264.35, -161.47) * mm, "end": v(637.65, -159.48) * mm});
            skLineSegment(sketch, "E251.2.1.1", {"start": v(-264.14, -180.52) * mm, "end": v(638.05, -178.53) * mm});
            skLineSegment(sketch, "E251.2.2.0", {"start": v(-264.35, -35.74) * mm, "end": v(637.65, -33.75) * mm});
            skLineSegment(sketch, "E251.2.2.1", {"start": v(-264.14, -54.8) * mm, "end": v(638.05, -52.8) * mm});
            skLineSegment(sketch, "E251.2.3.0", {"start": v(-264.35, 89.99) * mm, "end": v(637.65, 91.98) * mm});
            skLineSegment(sketch, "E251.2.3.1", {"start": v(-264.14, 70.94) * mm, "end": v(638.05, 72.93) * mm});
            skLineSegment(sketch, "E251.2.4.0", {"start": v(-264.35, 215.72) * mm, "end": v(637.65, 217.7) * mm});
            skLineSegment(sketch, "E251.2.4.1", {"start": v(-264.14, 196.67) * mm, "end": v(638.05, 198.66) * mm});
            skLineSegment(sketch, "E251.2.5.0", {"start": v(-264.35, 341.45) * mm, "end": v(637.65, 343.44) * mm});
            skLineSegment(sketch, "E251.2.5.1", {"start": v(-264.14, 322.4) * mm, "end": v(638.05, 324.39) * mm});
            skLineSegment(sketch, "E251.direction1", {"start": v(-315.15, -287.2) * mm, "end": v(-289.75, -287.2) * mm, "construction": true});
            skLineSegment(sketch, "E251.direction2", {"start": v(-315.15, -287.2) * mm, "end": v(-315.15, -161.47) * mm, "construction": true});
            skLineSegment(sketch, "E252", {"start": v(637.65, 343.44) * mm, "end": v(835.9, 343.44) * mm});
            skLineSegment(sketch, "E253", {"start": v(638.05, 324.39) * mm, "end": v(835.9, 324.39) * mm});
            skLineSegment(sketch, "E254", {"start": v(637.65, 217.7) * mm, "end": v(835.9, 217.7) * mm});
            skLineSegment(sketch, "E255", {"start": v(638.05, 198.66) * mm, "end": v(835.9, 198.66) * mm});
            skLineSegment(sketch, "E256", {"start": v(637.65, 91.98) * mm, "end": v(835.9, 91.98) * mm});
            skLineSegment(sketch, "E257", {"start": v(638.05, 72.93) * mm, "end": v(826.9, 72.93) * mm});
            skLineSegment(sketch, "E258", {"start": v(637.65, -33.75) * mm, "end": v(755.47, -33.75) * mm});
            skLineSegment(sketch, "E259", {"start": v(638.05, -52.8) * mm, "end": v(742.71, -52.8) * mm});
            skLineSegment(sketch, "E260", {"start": v(637.65, -159.48) * mm, "end": v(671.29, -159.48) * mm});
            skLineSegment(sketch, "E261", {"start": v(638.05, -178.53) * mm, "end": v(658.53, -178.53) * mm});
            skLineSegment(sketch, "E262", {"start": v(-315.15, 341.45) * mm, "end": v(-586.5, 341.45) * mm});
            skLineSegment(sketch, "E263", {"start": v(-314.94, 322.4) * mm, "end": v(-586.5, 322.4) * mm});
            skLineSegment(sketch, "E264", {"start": v(-315.15, 215.72) * mm, "end": v(-586.5, 215.72) * mm});
            skLineSegment(sketch, "E265", {"start": v(-314.94, 196.67) * mm, "end": v(-586.5, 196.67) * mm});
            skLineSegment(sketch, "E266", {"start": v(-315.15, 89.99) * mm, "end": v(-586.5, 89.99) * mm});
            skLineSegment(sketch, "E267", {"start": v(-314.94, 70.94) * mm, "end": v(-578.9, 70.94) * mm});
            skLineSegment(sketch, "E268", {"start": v(-315.15, -35.74) * mm, "end": v(-500.27, -35.74) * mm});
            skLineSegment(sketch, "E269", {"start": v(-314.94, -54.8) * mm, "end": v(-486.24, -54.8) * mm});
            skLineSegment(sketch, "E270", {"start": v(-315.15, -161.47) * mm, "end": v(-407.62, -161.47) * mm});
            skLineSegment(sketch, "E271", {"start": v(-314.94, -180.52) * mm, "end": v(-393.58, -180.52) * mm});
            skLineSegment(sketch, "E272.trimOffspring", {"start": v(-307.99, -306.24) * mm, "end": v(-310.7, -1058.45) * mm});
            skLineSegment(sketch, "E273.trimOffspring", {"start": v(-287.88, -306.2) * mm, "end": v(-287.88, -1056.63) * mm});
            skLineSegment(sketch, "E274.trimOffspring", {"start": v(-162.15, -305.91) * mm, "end": v(-162.15, -1056.63) * mm});
            skLineSegment(sketch, "E275.trimOffspring", {"start": v(-143.1, -305.87) * mm, "end": v(-143.1, -1056.63) * mm});
            skLineSegment(sketch, "E276.trimOffspring", {"start": v(-17.37, -305.6) * mm, "end": v(-17.37, -1056.63) * mm});
            skLineSegment(sketch, "E277.trimOffspring", {"start": v(1.68, -305.55) * mm, "end": v(1.68, -1056.63) * mm});
            skLineSegment(sketch, "E278.trimOffspring", {"start": v(127.41, -305.28) * mm, "end": v(127.41, -1056.63) * mm});
            skLineSegment(sketch, "E279.trimOffspring", {"start": v(146.46, -305.23) * mm, "end": v(146.46, -1056.63) * mm});
            skLineSegment(sketch, "E280.trimOffspring", {"start": v(272.2, -304.96) * mm, "end": v(272.2, -1056.63) * mm});
            skLineSegment(sketch, "E281.trimOffspring", {"start": v(291.24, -304.92) * mm, "end": v(291.24, -1056.63) * mm});
            skLineSegment(sketch, "E282.trimOffspring", {"start": v(416.97, -304.64) * mm, "end": v(416.97, -1056.63) * mm});
            skLineSegment(sketch, "E283.trimOffspring", {"start": v(436.02, -304.6) * mm, "end": v(436.02, -1056.63) * mm});
            skLineSegment(sketch, "E284.trimOffspring", {"start": v(561.75, -304.32) * mm, "end": v(561.75, -1056.63) * mm});
            skLineSegment(sketch, "E285.trimOffspring", {"start": v(580.8, -304.28) * mm, "end": v(580.8, -1056.63) * mm});
            skLineSegment(sketch, "E286", {"start": v(-289.75, -287.2) * mm, "end": v(-315.15, -287.2) * mm});
            skPoint(sketch, "E287.orphan", {"position": v(612.25, -285.21) * mm});
            skPoint(sketch, "E288.orphan", {"position": v(637.65, -285.21) * mm});
            skPoint(sketch, "E289.orphan", {"position": v(612.65, -304.26) * mm});
            skPoint(sketch, "E290.orphan", {"position": v(638.05, -304.26) * mm});
            skLineSegment(sketch, "E291", {"start": v(-586.5, 341.45) * mm, "end": v(835.9, 343.44) * mm});
            skLineSegment(sketch, "E292", {"start": v(-586.5, 322.4) * mm, "end": v(835.9, 324.39) * mm});
            skLineSegment(sketch, "E293", {"start": v(-586.5, 215.72) * mm, "end": v(835.9, 217.7) * mm});
            skLineSegment(sketch, "E294", {"start": v(835.9, 198.66) * mm, "end": v(-586.5, 196.67) * mm});
            skLineSegment(sketch, "E295", {"start": v(-586.5, 89.99) * mm, "end": v(835.9, 91.98) * mm});
            skLineSegment(sketch, "E296", {"start": v(-578.9, 70.94) * mm, "end": v(826.9, 72.93) * mm});
            skLineSegment(sketch, "E297", {"start": v(-500.27, -35.74) * mm, "end": v(755.47, -33.75) * mm});
            skLineSegment(sketch, "E298", {"start": v(742.71, -52.8) * mm, "end": v(-486.24, -54.8) * mm});
            skLineSegment(sketch, "E299", {"start": v(-500.27, -35.74) * mm, "end": v(-486.24, -54.8) * mm});
            skLineSegment(sketch, "E300", {"start": v(755.47, -33.75) * mm, "end": v(742.71, -52.8) * mm});
            skLineSegment(sketch, "E301", {"start": v(-407.62, -161.47) * mm, "end": v(671.29, -159.48) * mm});
            skLineSegment(sketch, "E302", {"start": v(658.53, -178.53) * mm, "end": v(-393.58, -180.52) * mm});
            skSolve(sketch);
        }
        {
            var Q0;
            {var subQ44=sQuery(id+"F7.wireOp",EDGE,"E206.0");Q0=makeQuery(id+"F7.imprint","IMPRINT",FACE,{"disambiguationData":[TD([[makeQuery(id+"F7.imprint","IMPRINT",EDGE,{"derivedFrom":subQ44}),-1.0]])]});}
            extrude(context, id + "F8", {"entities" : qUnion([Q0]), "depth" : 50.8 * mm, "offsetDistance" : 25.4 * mm});
        }
        {
            var Q0;
            {var subQ0=sQuery(id+"F7.wireOp",EDGE,"E240.trimOffspring");Q0=makeQuery(id+"F7.imprint","IMPRINT",FACE,{"disambiguationData":[TD([[makeQuery(id+"F7.imprint","IMPRINT",EDGE,{"derivedFrom":subQ0}),-1.0]])]});}
            var Q1;
            {var subQ0=sQuery(id+"F7.wireOp",EDGE,"E230.trimOffspring");Q1=makeQuery(id+"F7.imprint","IMPRINT",FACE,{"disambiguationData":[TD([[makeQuery(id+"F7.imprint","IMPRINT",EDGE,{"derivedFrom":subQ0}),-1.0]])]});}
            var Q2;
            {var subQ0=sQuery(id+"F7.wireOp",EDGE,"E274.trimOffspring");var subQ1=sQuery(id+"F7.wireOp",EDGE,"E205.2");var subQ2=makeQuery(id+"F7.imprint","INTERSECT",VERTEX,{"derivedFrom":[subQ1,subQ0]});Q2=makeQuery(id+"F7.imprint","IMPRINT",FACE,{"disambiguationData":[TD([[makeQuery(id+"F7.imprint","IMPRINT",EDGE,{"disambiguationData":[TD([[subQ2,-1.0]])],"derivedFrom":subQ1}),1.0]])]});}
            var Q3;
            {var subQ0=sQuery(id+"F7.wireOp",EDGE,"E276.trimOffspring");var subQ1=sQuery(id+"F7.wireOp",EDGE,"E205.2");var subQ2=makeQuery(id+"F7.imprint","INTERSECT",VERTEX,{"derivedFrom":[subQ1,subQ0]});Q3=makeQuery(id+"F7.imprint","IMPRINT",FACE,{"disambiguationData":[TD([[makeQuery(id+"F7.imprint","IMPRINT",EDGE,{"disambiguationData":[TD([[subQ2,-1.0]])],"derivedFrom":subQ1}),1.0]])]});}
            var Q4;
            {var subQ0=sQuery(id+"F7.wireOp",EDGE,"E278.trimOffspring");var subQ1=sQuery(id+"F7.wireOp",EDGE,"E205.2");var subQ2=makeQuery(id+"F7.imprint","INTERSECT",VERTEX,{"derivedFrom":[subQ1,subQ0]});Q4=makeQuery(id+"F7.imprint","IMPRINT",FACE,{"disambiguationData":[TD([[makeQuery(id+"F7.imprint","IMPRINT",EDGE,{"disambiguationData":[TD([[subQ2,-1.0]])],"derivedFrom":subQ1}),1.0]])]});}
            var Q5;
            {var subQ0=sQuery(id+"F7.wireOp",EDGE,"E280.trimOffspring");var subQ1=sQuery(id+"F7.wireOp",EDGE,"E205.2");var subQ2=makeQuery(id+"F7.imprint","INTERSECT",VERTEX,{"derivedFrom":[subQ1,subQ0]});Q5=makeQuery(id+"F7.imprint","IMPRINT",FACE,{"disambiguationData":[TD([[makeQuery(id+"F7.imprint","IMPRINT",EDGE,{"disambiguationData":[TD([[subQ2,-1.0]])],"derivedFrom":subQ1}),1.0]])]});}
            var Q6;
            {var subQ0=sQuery(id+"F7.wireOp",EDGE,"E282.trimOffspring");var subQ1=sQuery(id+"F7.wireOp",EDGE,"E205.2");var subQ2=makeQuery(id+"F7.imprint","INTERSECT",VERTEX,{"derivedFrom":[subQ1,subQ0]});Q6=makeQuery(id+"F7.imprint","IMPRINT",FACE,{"disambiguationData":[TD([[makeQuery(id+"F7.imprint","IMPRINT",EDGE,{"disambiguationData":[TD([[subQ2,-1.0]])],"derivedFrom":subQ1}),1.0]])]});}
            var Q7;
            {var subQ0=sQuery(id+"F7.wireOp",EDGE,"E284.trimOffspring");var subQ1=sQuery(id+"F7.wireOp",EDGE,"E205.2");var subQ2=makeQuery(id+"F7.imprint","INTERSECT",VERTEX,{"derivedFrom":[subQ1,subQ0]});Q7=makeQuery(id+"F7.imprint","IMPRINT",FACE,{"disambiguationData":[TD([[makeQuery(id+"F7.imprint","IMPRINT",EDGE,{"disambiguationData":[TD([[subQ2,-1.0]])],"derivedFrom":subQ1}),1.0]])]});}
            var Q8;
            {var subQ3=sQuery(id+"F7.wireOp",EDGE,"E205.2");var subQ5=sQuery(id+"F7.wireOp",EDGE,"E273.trimOffspring");var subQ8=makeQuery(id+"F7.imprint","INTERSECT",VERTEX,{"derivedFrom":[subQ3,subQ5]});Q8=makeQuery(id+"F7.imprint","IMPRINT",FACE,{"disambiguationData":[TD([[makeQuery(id+"F7.imprint","IMPRINT",EDGE,{"disambiguationData":[TD([[subQ8,1.0]])],"derivedFrom":subQ3}),1.0]])]});}
            var Q9;
            {var subQ9=sQuery(id+"F7.wireOp",EDGE,"E251.1.0.0");Q9=makeQuery(id+"F7.imprint","IMPRINT",FACE,{"disambiguationData":[TD([[makeQuery(id+"F7.imprint","IMPRINT",EDGE,{"derivedFrom":subQ9}),-1.0]])]});}
            extrude(context, id + "F9", {"entities" : qUnion([Q0, Q1, Q2, Q3, Q4, Q5, Q6, Q7, Q8, Q9]), "operationType" : NewBodyOperationType.ADD, "depth" : 19.05 * mm, "offsetDistance" : 25.4 * mm});
        }
        {
            var Q0;
            {var subQ5=sQuery(id+"F7.wireOp",EDGE,"E253");Q0=makeQuery(id+"F7.imprint","IMPRINT",FACE,{"disambiguationData":[TD([[makeQuery(id+"F7.imprint","IMPRINT",EDGE,{"derivedFrom":subQ5}),1.0]])]});}
            var Q1;
            {var subQ4=sQuery(id+"F7.wireOp",EDGE,"E255");Q1=makeQuery(id+"F7.imprint","IMPRINT",FACE,{"disambiguationData":[TD([[makeQuery(id+"F7.imprint","IMPRINT",EDGE,{"derivedFrom":subQ4}),1.0]])]});}
            var Q2;
            {var subQ5=sQuery(id+"F7.wireOp",EDGE,"E257");Q2=makeQuery(id+"F7.imprint","IMPRINT",FACE,{"disambiguationData":[TD([[makeQuery(id+"F7.imprint","IMPRINT",EDGE,{"derivedFrom":subQ5}),1.0]])]});}
            var Q3;
            {var subQ12=sQuery(id+"F7.wireOp",EDGE,"E259");Q3=makeQuery(id+"F7.imprint","IMPRINT",FACE,{"disambiguationData":[TD([[makeQuery(id+"F7.imprint","IMPRINT",EDGE,{"derivedFrom":subQ12}),1.0]])]});}
            var Q4;
            {var subQ11=sQuery(id+"F7.wireOp",EDGE,"E261");Q4=makeQuery(id+"F7.imprint","IMPRINT",FACE,{"disambiguationData":[TD([[makeQuery(id+"F7.imprint","IMPRINT",EDGE,{"derivedFrom":subQ11}),1.0]])]});}
            extrude(context, id + "F10", {"entities" : qUnion([Q0, Q1, Q2, Q3, Q4]), "operationType" : NewBodyOperationType.ADD, "depth" : 19.05 * mm, "offsetDistance" : 25.4 * mm});
        }
    });
